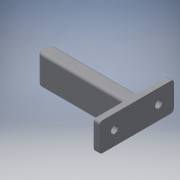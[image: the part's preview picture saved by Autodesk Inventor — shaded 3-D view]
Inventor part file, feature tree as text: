
AUTODESK INVENTOR PART (.ipt)
format: ipt  version: 2018 (Build 220112000, 112)  size: 185,856 bytes
history: native  units: mm
features: other x5, reference x4, extrude x3, sketch x3, plane x1, fillet x1
ambient origin geometry x8: Origin, YZ Plane, XZ Plane, XY Plane, X Axis, Y Axis, Z Axis, Center Point
bodies: Solid1 (feature_tree)
feature tree (17):
  extrude  "Extrusion1"  Depth=10.0mm TaperAngle=0.0deg
  sketch  "Sketch2"  dims[d4=2.5mm d5=2.5mm]
  plane  "Work Plane1"
  extrude  "Extrusion2"  Depth=2.5mm
  extrude  "Extrusion3"  Depth=1.0mm
  fillet  "Fillet1"  [1 undecoded]
  sketch  "Sketch1"  dims[d0=10.0mm d1=0.0mm d2=10.0mm d3=0.0mm]
  reference  "Reference1"
  reference  "Reference2"
  reference  "Reference3"
  sketch  "Sketch3"  dims[d6=2.0mm d7=0.0mm d8=1.0mm]
  reference  "Reference4"
  other  "<userpath>\OneDrive\Documents\Inventor\TSA\2018\Animatronics\Tortoise\AssemblyTURTLE.iam"
  other  "AssemblyTURTLE.iam"
  other  "GuideArm:1"
  other  "Frame - Copy:1"
  other  "Supporter:1"
note: 1 required parameter value undecoded (feature->parameter linkage not recoverable at this tier; creation-order binding heuristic only, values carry confidence <= 0.55)
